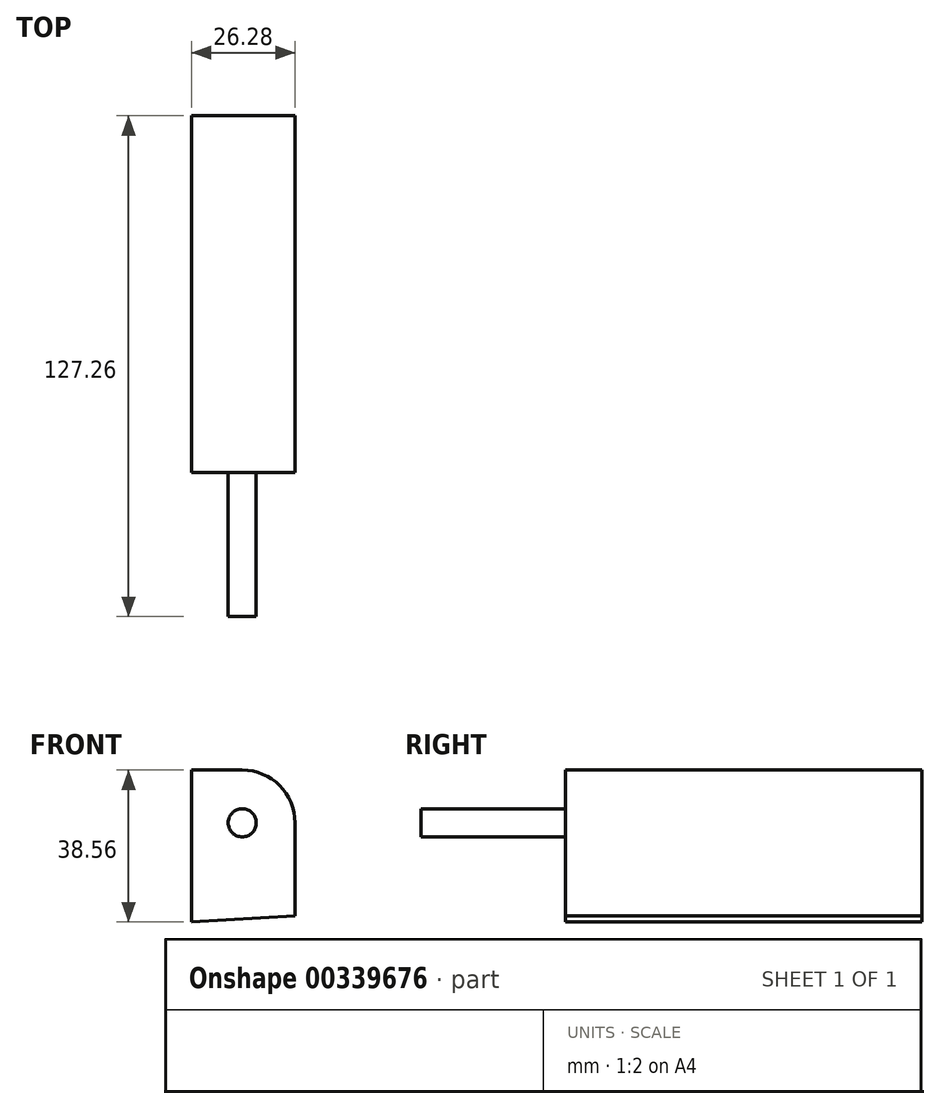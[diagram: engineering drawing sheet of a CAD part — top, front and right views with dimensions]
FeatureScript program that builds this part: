
annotation { "Feature Type Name" : "Feature", "Feature Type Description" : "" }
export const myFeature = defineFeature(function(context is Context, id is Id, definition is map)
    precondition{}
    {
        {
            var Q0;
            Q0=qCreatedBy(makeId("Front.planeOp"),FACE);
            var sketch = newSketch(context, id + "F0", { "sketchPlane" : qUnion([Q0])});
            skLineSegment(sketch, "E0.bottom", {"start": v(-42.56, 38.56) * mm, "end": v(36.84, 38.56) * mm});
            skLineSegment(sketch, "E0.top", {"start": v(-42.56, -47.66) * mm, "end": v(36.84, -47.66) * mm});
            skLineSegment(sketch, "E0.left", {"start": v(-42.56, 38.56) * mm, "end": v(-42.56, -47.66) * mm});
            skLineSegment(sketch, "E0.right", {"start": v(36.84, 38.56) * mm, "end": v(36.84, -47.66) * mm});
            skLineSegment(sketch, "E1", {"start": v(36.84, 38.56) * mm, "end": v(91.24, 96.7) * mm});
            skLineSegment(sketch, "E2", {"start": v(91.24, 96.7) * mm, "end": v(10.56, 96.7) * mm});
            skLineSegment(sketch, "E3", {"start": v(10.56, 96.7) * mm, "end": v(-42.56, 38.56) * mm});
            skLineSegment(sketch, "E4", {"start": v(91.24, 4.8) * mm, "end": v(91.24, 96.7) * mm});
            skLineSegment(sketch, "E5", {"start": v(91.24, 4.8) * mm, "end": v(36.84, -47.66) * mm});
            skLineSegment(sketch, "E6", {"start": v(10.56, 0) * mm, "end": v(10.56, 96.7) * mm});
            skLineSegment(sketch, "E7", {"start": v(-42.56, -47.66) * mm, "end": v(10.56, 0) * mm});
            skLineSegment(sketch, "E8", {"start": v(91.24, 4.8) * mm, "end": v(10.56, 0) * mm});
            skSolve(sketch);
        }
        {
            var Q0;
            {var subQ1=sQuery(id+"F0.wireOp",EDGE,"E0.bottom");var subQ3=sQuery(id+"F0.wireOp",EDGE,"E6");var subQ4=makeQuery(id+"F0.imprint","INTERSECT",VERTEX,{"derivedFrom":[subQ1,subQ3]});Q0=makeQuery(id+"F0.imprint","IMPRINT",FACE,{"disambiguationData":[TD([[makeQuery(id+"F0.imprint","IMPRINT",EDGE,{"disambiguationData":[TD([[subQ4,-1.0]])],"derivedFrom":subQ1}),-1.0]])]});}
            extrude(context, id + "F1", {"entities" : qUnion([Q0]), "depth" : 90.6 * mm});
        }
        {
            var Q0;
            Q0=makeQuery(id+"F1.opExtrude","SWEPT_EDGE",EDGE,{"disambiguationData":[OSD([sQuery(id+"F0.wireOp",EDGE,"E0.bottom"),sQuery(id+"F0.wireOp",EDGE,"E0.right"),sQuery(id+"F0.wireOp",EDGE,"E1")])]});
            fillet(context, id + "F2", {"entities" : qUnion([Q0]), "radius" : 13.4 * mm, "tangentPropagation" : true, "allowEdgeOverflow" : false});
        }
        {
            var Q0;
            Q0=makeQuery(id+"F1.opExtrude","CAP_FACE",FACE,{"disambiguationData":[OSD([sQuery(id+"F0.wireOp",EDGE,"E0.bottom"),sQuery(id+"F0.wireOp",EDGE,"E0.right"),sQuery(id+"F0.wireOp",EDGE,"E6"),sQuery(id+"F0.wireOp",EDGE,"E8")])],"isStart":false});
            var sketch = newSketch(context, id + "F3", { "sketchPlane" : qUnion([Q0])});
            skCircle(sketch, "E9", {"center": v(23.44, 25.16) * mm, "radius": 3.57 * mm});
            skSolve(sketch);
        }
        {
            var Q0;
            Q0 = qSketchRegion(id + "F3", true);
            extrude(context, id + "F4", {"entities" : qUnion([Q0]), "operationType" : NewBodyOperationType.ADD, "depth" : 36.66 * mm});
        }
    });
